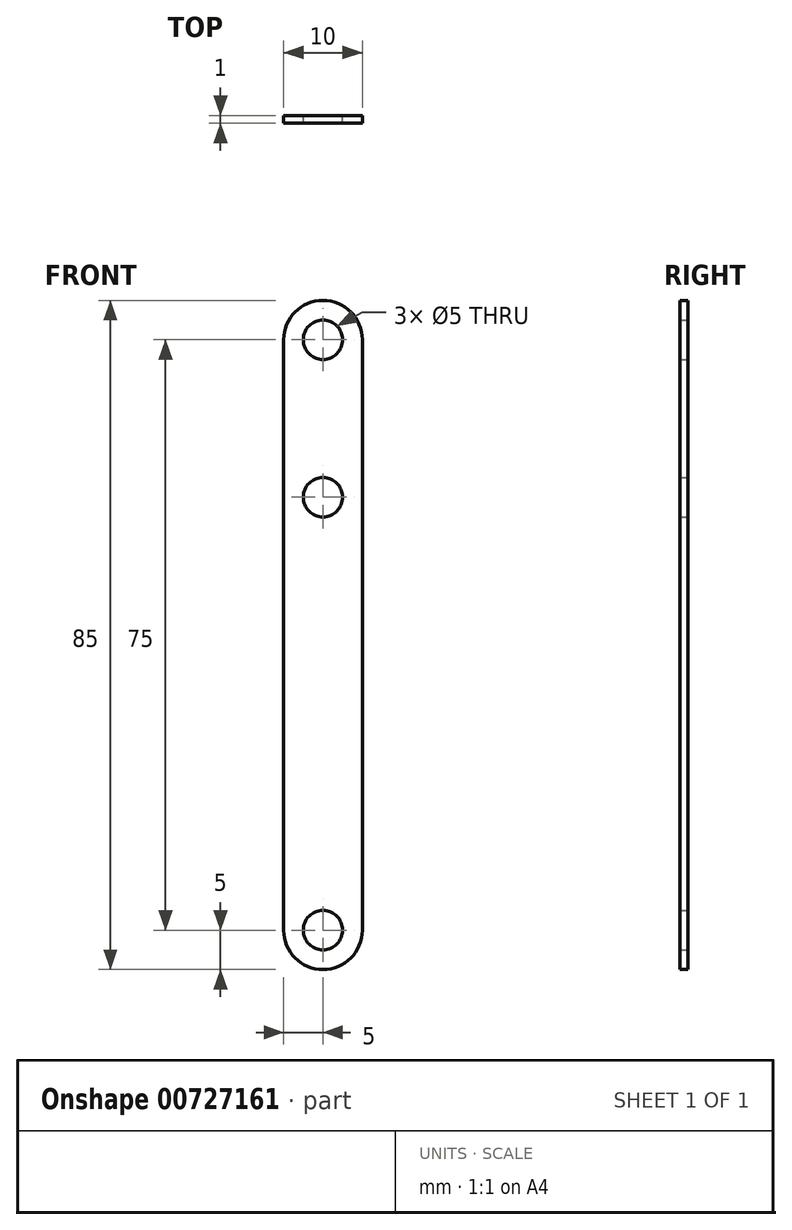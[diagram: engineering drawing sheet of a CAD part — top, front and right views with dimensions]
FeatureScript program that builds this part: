
annotation { "Feature Type Name" : "Feature", "Feature Type Description" : "" }
export const myFeature = defineFeature(function(context is Context, id is Id, definition is map)
    precondition{}
    {
        {
            var Q0;
            Q0=qCreatedBy(makeId("Front.planeOp"),FACE);
            var sketch = newSketch(context, id + "F0", { "sketchPlane" : qUnion([Q0])});
            skArc(sketch, "E0", {"start": v(5, 37.5) * mm, "mid": v(0, 42.5) * mm, "end": v(-5, 37.5) * mm});
            skArc(sketch, "E1", {"start": v(-5, -37.5) * mm, "mid": v(0, -42.5) * mm, "end": v(5, -37.5) * mm});
            skCircle(sketch, "E2", {"center": v(0, 37.5) * mm, "radius": 2.5 * mm});
            skCircle(sketch, "E3", {"center": v(0, -37.5) * mm, "radius": 2.5 * mm});
            skLineSegment(sketch, "E4", {"start": v(-5, 37.5) * mm, "end": v(-5, -37.5) * mm});
            skLineSegment(sketch, "E5", {"start": v(5, 37.5) * mm, "end": v(5, -37.5) * mm});
            skCircle(sketch, "E6", {"center": v(0, 17.5) * mm, "radius": 2.5 * mm});
            skSolve(sketch);
        }
        {
            var Q0;
            Q0=makeQuery(id+"F0.imprint","IMPRINT",FACE,{"disambiguationData":[TD([[makeQuery(id+"F0.imprint","IMPRINT",EDGE,{"derivedFrom":sQuery(id+"F0.wireOp",EDGE,"E0")}),1.0]])]});
            extrude(context, id + "F1", {"entities" : qUnion([Q0]), "depth" : 1 * mm, "offsetDistance" : 25.4 * mm});
        }
    });
